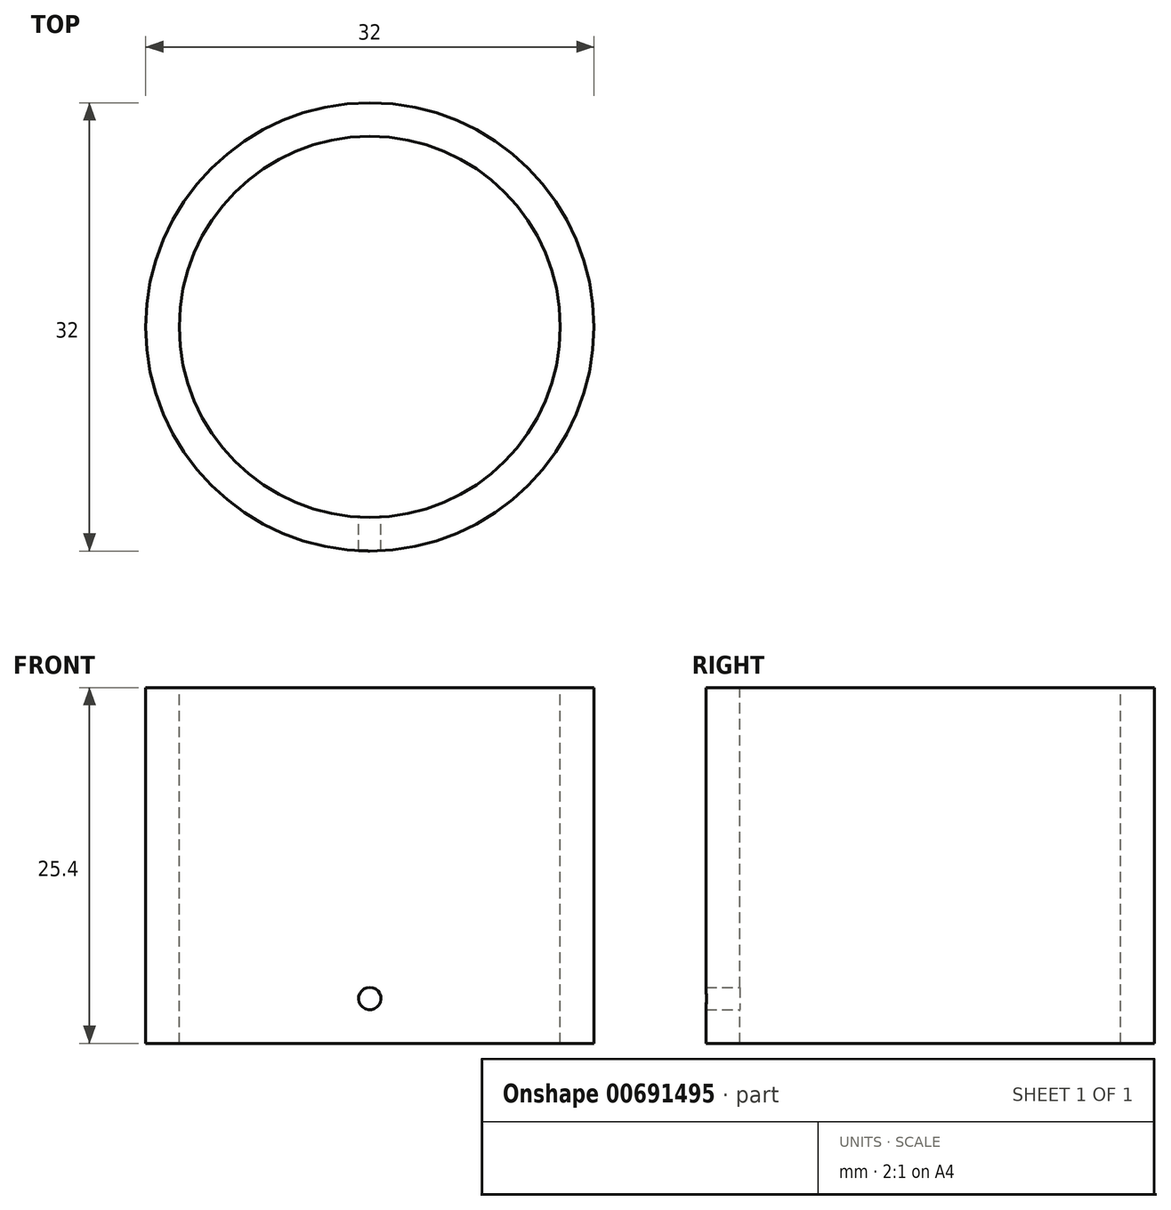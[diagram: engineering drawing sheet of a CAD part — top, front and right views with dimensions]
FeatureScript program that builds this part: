
annotation { "Feature Type Name" : "Feature", "Feature Type Description" : "" }
export const myFeature = defineFeature(function(context is Context, id is Id, definition is map)
    precondition{}
    {
        {
            var Q0;
            Q0=qCreatedBy(makeId("Front.planeOp"),FACE);
            var sketch = newSketch(context, id + "F0", { "sketchPlane" : qUnion([Q0])});
            skLineSegment(sketch, "E0", {"start": v(-16, 0) * mm, "end": v(-16, 25.4) * mm});
            skLineSegment(sketch, "E1", {"start": v(-16, 25.4) * mm, "end": v(-13.6, 25.4) * mm});
            skLineSegment(sketch, "E2", {"start": v(-13.6, 25.4) * mm, "end": v(-13.6, 0) * mm});
            skLineSegment(sketch, "E3", {"start": v(-13.6, 0) * mm, "end": v(-16, 0) * mm});
            skLineSegment(sketch, "E4", {"start": v(0, 0) * mm, "end": v(0, -17.74) * mm});
            skSolve(sketch);
        }
        {
            var Q0;
            Q0 = qSketchRegion(id + "F0", true);
            var Q1;
            Q1=sQuery(id+"F0.wireOp",EDGE,"E4");
            revolve(context, id + "F1", {"entities" : qUnion([Q0]), "axis" : qUnion([Q1]), "revolveType" : RevolveType.FULL});
        }
        {
            var Q0;
            Q0=qCreatedBy(makeId("Front.planeOp"),FACE);
            var sketch = newSketch(context, id + "F2", { "sketchPlane" : qUnion([Q0])});
            skCircle(sketch, "E5", {"center": v(0, 3.2) * mm, "radius": 0.8 * mm});
            skSolve(sketch);
        }
        {
            var Q0;
            Q0 = qSketchRegion(id + "F2", true);
            extrude(context, id + "F3", {"entities" : qUnion([Q0]), "operationType" : NewBodyOperationType.REMOVE, "depth" : 40 * mm, "offsetDistance" : 25 * mm});
        }
    });
